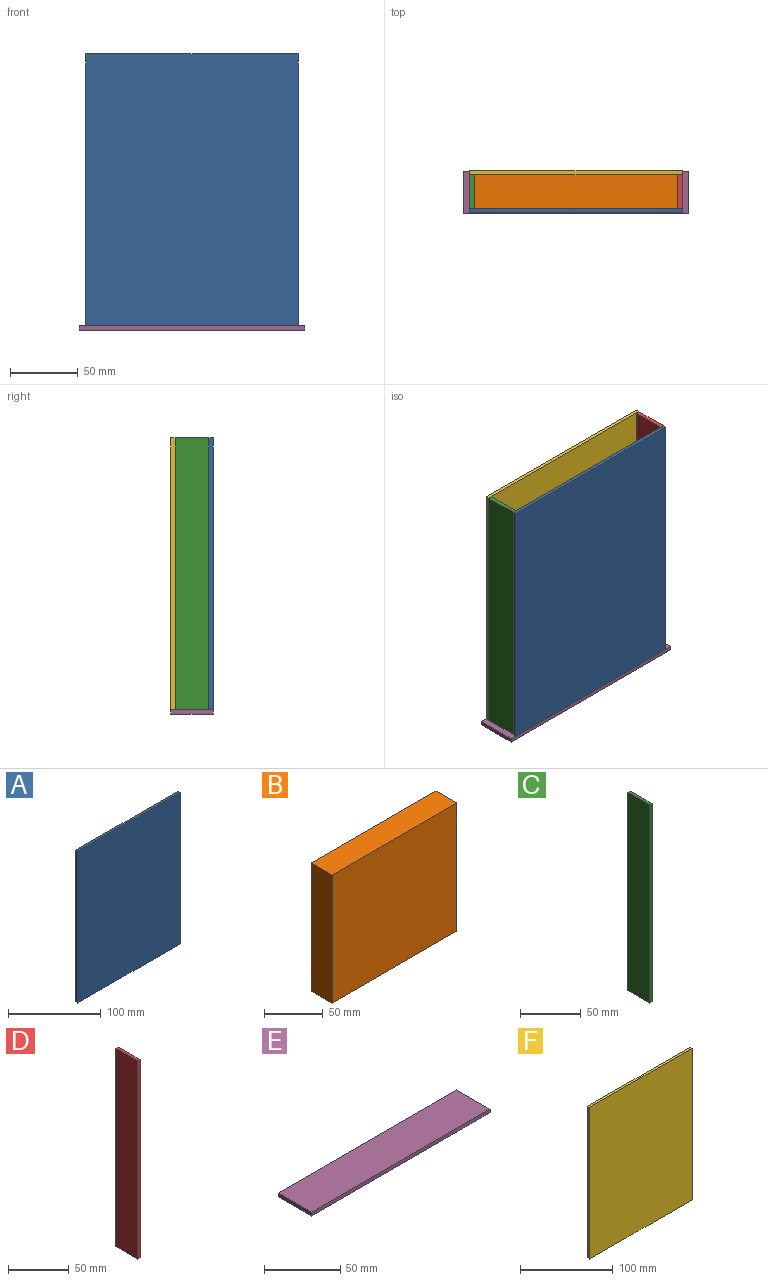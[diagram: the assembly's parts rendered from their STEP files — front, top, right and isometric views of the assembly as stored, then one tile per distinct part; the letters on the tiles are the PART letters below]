
ASSEMBLY  parts=6 mates=5
PART A: 6 faces, bbox 156x3x200 mm
  f0: plane 200x3mm, normal (-1,0,0), area 600mm2, adj f1,f3,f4,f5
  f1: plane 200x156mm, normal (0,-1,0), area 31200mm2, adj f0,f2,f4,f5
  f2: plane 200x3mm, normal (1,0,0), area 600mm2, adj f1,f3,f4,f5
  f3: plane 200x156mm, normal (0,1,0), area 31200mm2, adj f0,f2,f4,f5
  f4: plane 156x3mm, normal (0,0,1), area 468mm2, adj f0,f1,f2,f3
  f5: plane 156x3mm, normal (0,0,-1), area 468mm2, adj f0,f1,f2,f3
PART B: 6 faces, bbox 150x25x133.3 mm
  f0: plane 150x133.33mm, normal (0,1,0), area 20000mm2, adj f1,f3,f4,f5
  f1: plane 133.33x25mm, normal (-1,0,0), area 3333.3mm2, adj f0,f2,f4,f5
  f2: plane 150x133.33mm, normal (0,-1,0), area 20000mm2, adj f1,f3,f4,f5
  f3: plane 133.33x25mm, normal (1,0,0), area 3333.3mm2, adj f0,f2,f4,f5
  f4: plane 150x25mm, normal (0,0,1), area 3750mm2, adj f0,f1,f2,f3
  f5: plane 150x25mm, normal (0,0,-1), area 3750mm2, adj f0,f1,f2,f3
PART C: 6 faces, bbox 3x25x200 mm
  f0: plane 200x3mm, normal (0,-1,0), area 600mm2, adj f1,f3,f4,f5
  f1: plane 200x25mm, normal (1,0,0), area 5000mm2, adj f0,f2,f4,f5
  f2: plane 200x3mm, normal (0,1,0), area 600mm2, adj f1,f3,f4,f5
  f3: plane 200x25mm, normal (-1,0,0), area 5000mm2, adj f0,f2,f4,f5
  f4: plane 25x3mm, normal (0,0,1), area 75mm2, adj f0,f1,f2,f3
  f5: plane 25x3mm, normal (0,0,-1), area 75mm2, adj f0,f1,f2,f3
PART D: 6 faces, bbox 3x25x200 mm
  f0: plane 200x25mm, normal (-1,0,0), area 5000mm2, adj f1,f3,f4,f5
  f1: plane 200x3mm, normal (0,-1,0), area 600mm2, adj f0,f2,f4,f5
  f2: plane 200x25mm, normal (1,0,0), area 5000mm2, adj f1,f3,f4,f5
  f3: plane 200x3mm, normal (0,1,0), area 600mm2, adj f0,f2,f4,f5
  f4: plane 25x3mm, normal (0,0,1), area 75mm2, adj f0,f1,f2,f3
  f5: plane 25x3mm, normal (0,0,-1), area 75mm2, adj f0,f1,f2,f3
PART E: 6 faces, bbox 166x31x3 mm
  f0: plane 31x3mm, normal (1,0,0), area 93mm2, adj f1,f3,f4,f5
  f1: plane 166x3mm, normal (0,1,0), area 498mm2, adj f0,f2,f4,f5
  f2: plane 31x3mm, normal (-1,0,0), area 93mm2, adj f1,f3,f4,f5
  f3: plane 166x3mm, normal (0,-1,0), area 498mm2, adj f0,f2,f4,f5
  f4: plane 166x31mm, normal (0,0,1), area 5146mm2, adj f0,f1,f2,f3
  f5: plane 166x31mm, normal (0,0,-1), area 5146mm2, adj f0,f1,f2,f3
PART F: 6 faces, bbox 156x3x200 mm
  f0: plane 200x3mm, normal (-1,0,0), area 600mm2, adj f1,f3,f4,f5
  f1: plane 200x156mm, normal (0,-1,0), area 31200mm2, adj f0,f2,f4,f5
  f2: plane 200x3mm, normal (1,0,0), area 600mm2, adj f1,f3,f4,f5
  f3: plane 200x156mm, normal (0,1,0), area 31200mm2, adj f0,f2,f4,f5
  f4: plane 156x3mm, normal (0,0,1), area 468mm2, adj f0,f1,f2,f3
  f5: plane 156x3mm, normal (0,0,-1), area 468mm2, adj f0,f1,f2,f3
PLACE A at identity
PLACE B at identity
PLACE C at identity
PLACE D at identity
PLACE E at identity fixed
PLACE F at identity
MATE fastened B.f5 <-> E.f4  axis (0,0,-1) through (0,0,3)mm
MATE fastened F.f5 <-> E.f4  axis (0,0,-1) through (78,12.5,3)mm
MATE fastened C.f5 <-> E.f4  axis (0,0,-1) through (-78,-12.5,3)mm
MATE fastened D.f5 <-> E.f4  axis (0,0,-1) through (78,12.5,3)mm
MATE fastened A.f5 <-> E.f4  axis (0,0,-1) through (-78,-12.5,3)mm
